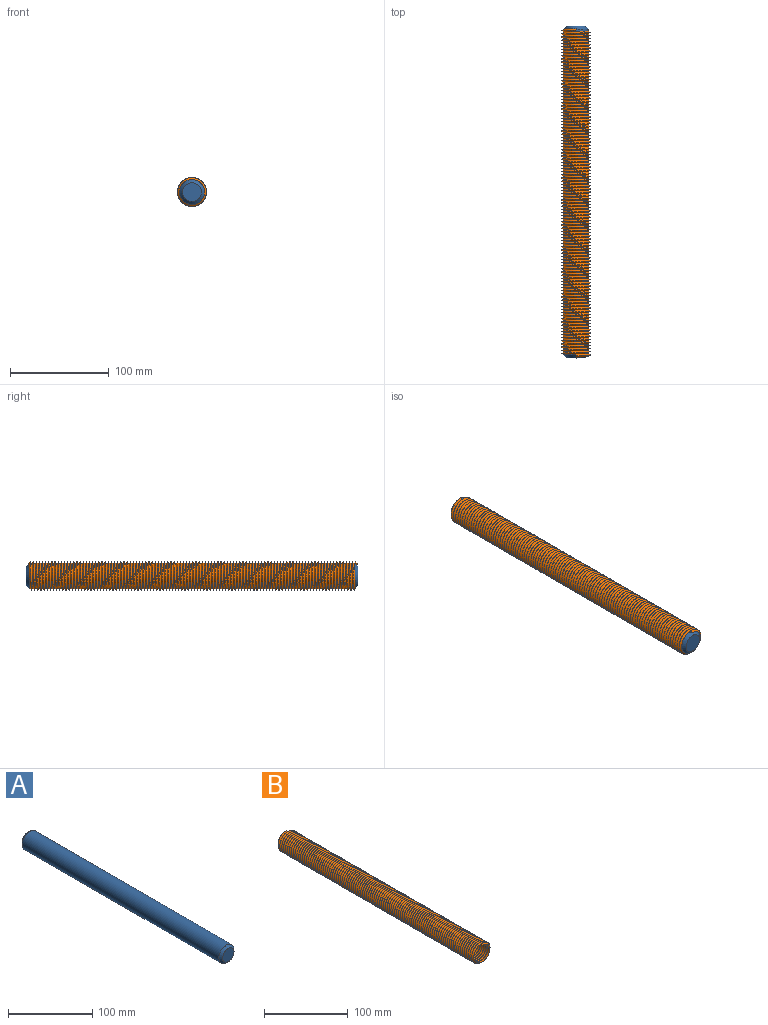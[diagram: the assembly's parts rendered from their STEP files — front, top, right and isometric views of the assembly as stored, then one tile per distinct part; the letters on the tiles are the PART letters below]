
ASSEMBLY  parts=2 mates=1
PART A: 5 faces, bbox 25.4x336.6x25.4 mm
  f0: cylinder r=12.7mm len=330.2mm, axis (0,1,0), area 26348.8mm2, adj f3,f4
  f1: plane 19.05x19.05mm, normal (0,-1,0), area 285mm2, adj f4
  f2: plane 19.05x19.05mm, normal (0,1,0), area 285mm2, adj f3
  f3: cone r=12.7mm half-angle=45deg, axis (0,-1,0), area 313.5mm2, adj f0,f2
  f4: cone r=9.53mm half-angle=45deg, axis (0,1,0), area 313.5mm2, adj f0,f1
PART B: 5 faces, bbox 33.5x333.2x29.1 mm
  f0: plane 3.01x1.82mm, normal (1,0,0), area 2.7mm2, adj f2,f3,f4
  f1: plane 3.01x1.82mm, normal (-1,0,0), area 2.7mm2, adj f2,f3,f4
  f2: bspline ~331.71x33.55mm, area 21069.4mm2, adj f0,f1,f3,f4
  f3: bspline ~331.71x33.55mm, area 21069.4mm2, adj f0,f1,f2,f4
  f4: cylinder r=12.7mm len=333.21mm, axis (0,-1,0), area 25025mm2, adj f0,f1,f2,f3
PLACE A t=(-77.78,89.83,-49.35)mm
PLACE B t=(-77.78,90.47,-49.35)mm
MATE fastened A.f0 <-> B.f4  axis (0,1,0) through (-77.78,89.83,-49.35)mm
